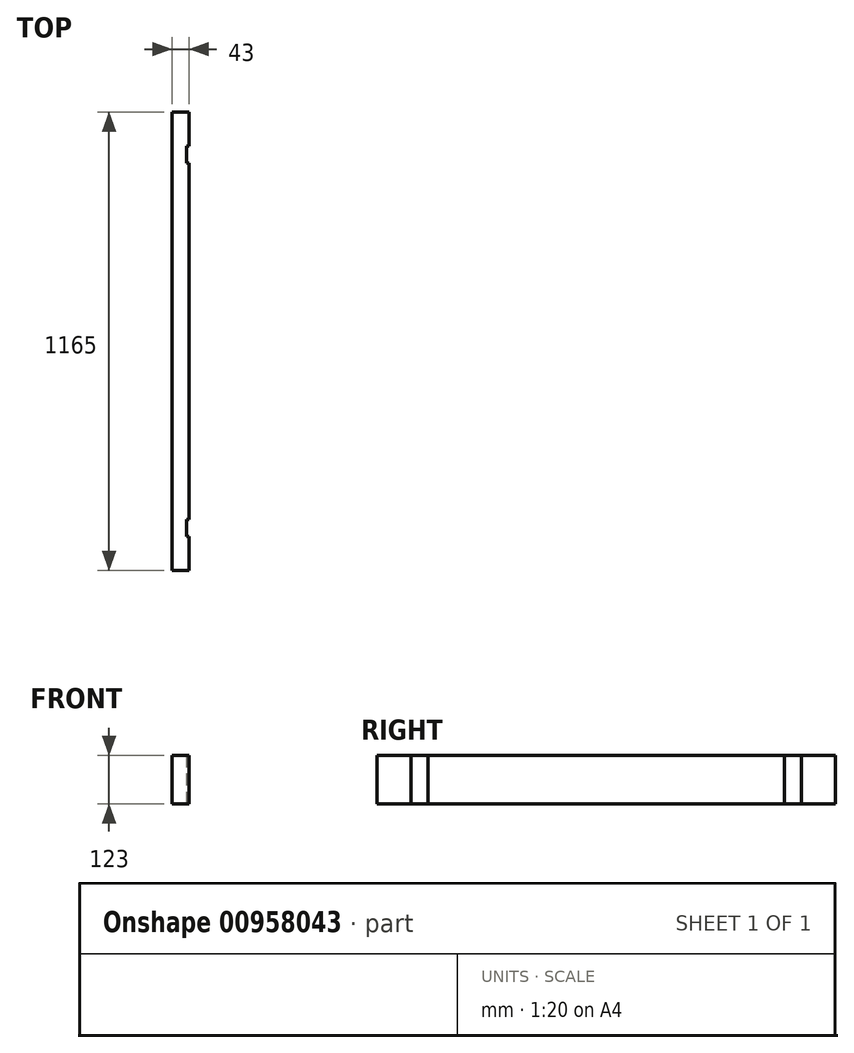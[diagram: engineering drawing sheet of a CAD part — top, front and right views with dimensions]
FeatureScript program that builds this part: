
annotation { "Feature Type Name" : "Feature", "Feature Type Description" : "" }
export const myFeature = defineFeature(function(context is Context, id is Id, definition is map)
    precondition{}
    {
        {
            var Q0;
            Q0=qCreatedBy(makeId("Front.planeOp"),FACE);
            var sketch = newSketch(context, id + "F0", { "sketchPlane" : qUnion([Q0])});
            skLineSegment(sketch, "E0.bottom", {"start": v(21.5, -66.39) * mm, "end": v(-21.5, -66.39) * mm});
            skLineSegment(sketch, "E0.top", {"start": v(21.5, 56.61) * mm, "end": v(-21.5, 56.61) * mm});
            skLineSegment(sketch, "E0.left", {"start": v(21.5, -66.39) * mm, "end": v(21.5, 56.61) * mm});
            skLineSegment(sketch, "E0.right", {"start": v(-21.5, -66.39) * mm, "end": v(-21.5, 56.61) * mm});
            skPoint(sketch, "E0.middle", {"position": v(0, -4.89) * mm});
            skSolve(sketch);
        }
        {
            var Q0;
            Q0=makeQuery(id+"F0.imprint","IMPRINT",FACE,{"disambiguationData":[TD([[makeQuery(id+"F0.imprint","IMPRINT",EDGE,{"derivedFrom":sQuery(id+"F0.wireOp",EDGE,"E0.bottom")}),-1.0]])]});
            extrude(context, id + "F1", {"entities" : qUnion([Q0]), "depth" : 1165 * mm, "offsetDistance" : 25 * mm});
        }
        {
            var Q0;
            Q0=makeQuery(id+"F1.opExtrude","SWEPT_FACE",FACE,{"disambiguationData":[OSD([sQuery(id+"F0.wireOp",EDGE,"E0.left")])]});
            var sketch = newSketch(context, id + "F2", { "sketchPlane" : qUnion([Q0])});
            skLineSegment(sketch, "E1.bottom", {"start": v(-1078, 56.61) * mm, "end": v(-1035, 56.61) * mm});
            skLineSegment(sketch, "E1.top", {"start": v(-1078, -66.39) * mm, "end": v(-1035, -66.39) * mm});
            skLineSegment(sketch, "E1.left", {"start": v(-1078, 56.61) * mm, "end": v(-1078, -66.39) * mm});
            skLineSegment(sketch, "E1.right", {"start": v(-1035, 56.61) * mm, "end": v(-1035, -66.39) * mm});
            skLineSegment(sketch, "E2", {"start": v(-582.5, 56.61) * mm, "end": v(-582.5, -66.39) * mm, "construction": true});
            skLineSegment(sketch, "E3.bottom", {"start": v(-130, 56.61) * mm, "end": v(-87, 56.61) * mm});
            skLineSegment(sketch, "E3.top", {"start": v(-130, -66.39) * mm, "end": v(-87, -66.39) * mm});
            skLineSegment(sketch, "E3.left", {"start": v(-130, 56.61) * mm, "end": v(-130, -66.39) * mm});
            skLineSegment(sketch, "E3.right", {"start": v(-87, 56.61) * mm, "end": v(-87, -66.39) * mm});
            skSolve(sketch);
        }
        {
            var Q0;
            Q0=makeQuery(id+"F2.imprint","IMPRINT",FACE,{"disambiguationData":[TD([[makeQuery(id+"F2.imprint","IMPRINT",EDGE,{"derivedFrom":sQuery(id+"F2.wireOp",EDGE,"E1.bottom")}),-1.0]])]});
            var Q1;
            Q1=makeQuery(id+"F2.imprint","IMPRINT",FACE,{"disambiguationData":[TD([[makeQuery(id+"F2.imprint","IMPRINT",EDGE,{"derivedFrom":sQuery(id+"F2.wireOp",EDGE,"E3.bottom")}),-1.0]])]});
            extrude(context, id + "F3", {"entities" : qUnion([Q0, Q1]), "operationType" : NewBodyOperationType.REMOVE, "oppositeDirection" : true, "depth" : 7 * mm, "offsetDistance" : 25 * mm});
        }
    });
